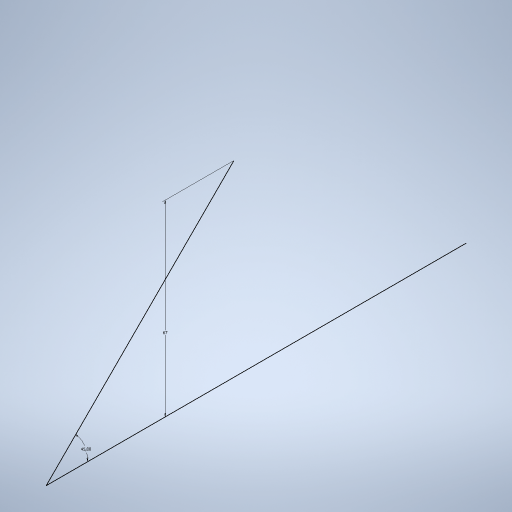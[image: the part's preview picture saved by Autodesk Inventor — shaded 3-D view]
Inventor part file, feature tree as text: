
AUTODESK INVENTOR PART (.ipt)
format: ipt  version: 2024.3 (Build 283343000, 343)  size: 231,424 bytes
history: native  units: mm
features: sketch x1
ambient origin geometry x8: Origin, YZ Plane, XZ Plane, XY Plane, X Axis, Y Axis, Z Axis, Center Point
feature tree (1):
  sketch  "Sketch2"  dims[d0=45.0deg d1=67.0mm]
